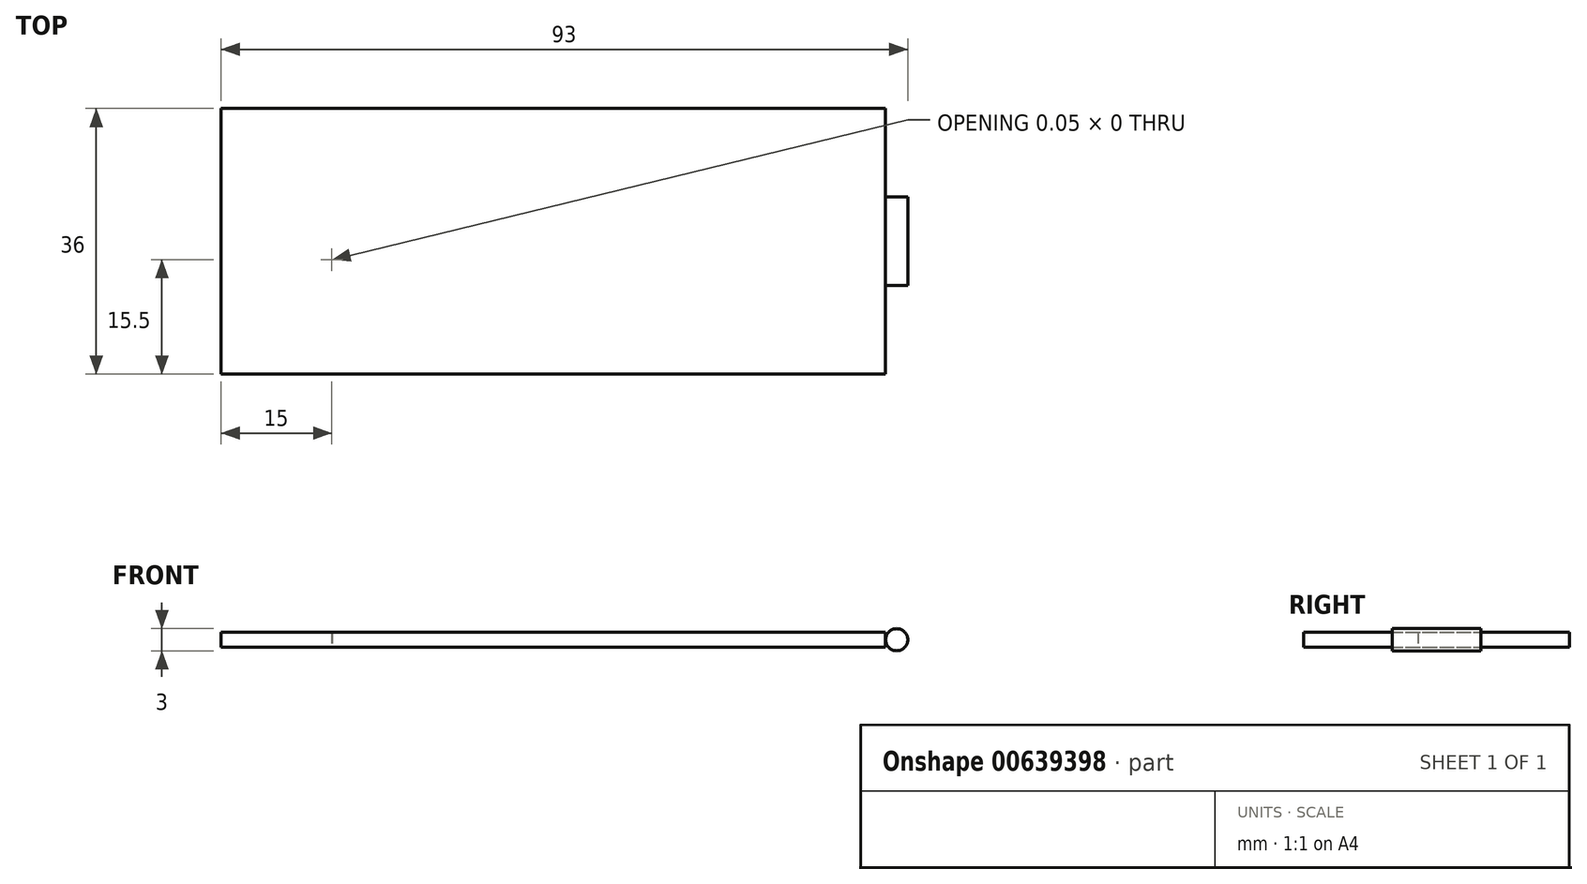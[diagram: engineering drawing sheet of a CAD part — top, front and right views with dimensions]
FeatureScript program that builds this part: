
annotation { "Feature Type Name" : "Feature", "Feature Type Description" : "" }
export const myFeature = defineFeature(function(context is Context, id is Id, definition is map)
    precondition{}
    {
        {
            var Q0;
            Q0=qCreatedBy(makeId("Top.planeOp"),FACE);
            var sketch = newSketch(context, id + "F0", { "sketchPlane" : qUnion([Q0])});
            skLineSegment(sketch, "E0.bottom", {"start": v(0, 0) * mm, "end": v(90, 0) * mm});
            skLineSegment(sketch, "E0.top", {"start": v(0, 36) * mm, "end": v(90, 36) * mm});
            skLineSegment(sketch, "E0.left", {"start": v(0, 0) * mm, "end": v(0, 36) * mm});
            skLineSegment(sketch, "E0.right", {"start": v(90, 0) * mm, "end": v(90, 36) * mm});
            skSolve(sketch);
        }
        {
            var Q0;
            Q0=makeQuery(id+"F0.imprint","IMPRINT",FACE,{"disambiguationData":[TD([[makeQuery(id+"F0.imprint","IMPRINT",EDGE,{"derivedFrom":sQuery(id+"F0.wireOp",EDGE,"E0.bottom")}),1.0]])]});
            extrude(context, id + "F1", {"entities" : qUnion([Q0]), "depth" : 2 * mm, "offsetDistance" : 25 * mm});
        }
        {
            var Q0;
            Q0=qCreatedBy(makeId("Front.planeOp"),FACE);
            cPlane(context, id + "F2", {"entities" : qUnion([Q0]), "cplaneType" : CPlaneType.OFFSET, "offset" : 18 * mm, "oppositeDirection" : true, "width" : 150 * mm, "height" : 150 * mm});
        }
        {
            var Q0;
            Q0=qCreatedBy(id+"F2.planeOp",FACE);
            var sketch = newSketch(context, id + "F3", { "sketchPlane" : qUnion([Q0])});
            skPoint(sketch, "E1.0", {"position": v(90, 1) * mm});
            skCircle(sketch, "E2", {"center": v(91.5, 1) * mm, "radius": 1.5 * mm});
            skSolve(sketch);
        }
        {
            var Q0;
            Q0=makeQuery(id+"F3.imprint","IMPRINT",FACE,{"disambiguationData":[TD([[makeQuery(id+"F3.imprint","IMPRINT",EDGE,{"derivedFrom":sQuery(id+"F3.wireOp",EDGE,"E2")}),1.0]])]});
            extrude(context, id + "F4", {"entities" : qUnion([Q0]), "operationType" : NewBodyOperationType.ADD, "depth" : 12 * mm, "offsetDistance" : 25 * mm, "symmetric" : true});
        }
        {
            var Q0;
            Q0=makeQuery(id+"F1.opExtrude","CAP_FACE",FACE,{"disambiguationData":[OSD([sQuery(id+"F0.wireOp",EDGE,"E0.bottom"),sQuery(id+"F0.wireOp",EDGE,"E0.top"),sQuery(id+"F0.wireOp",EDGE,"E0.left"),sQuery(id+"F0.wireOp",EDGE,"E0.right")])],"isStart":true});
            var sketch = newSketch(context, id + "F5", { "sketchPlane" : qUnion([Q0])});
            skLineSegment(sketch, "E3.0", {"start": v(0, 0) * mm, "end": v(0, -36) * mm});
            skArc(sketch, "E4", {"start": v(15.02, -15.5) * mm, "mid": v(12.5, -17.99) * mm, "end": v(15, -20.5) * mm});
            skPoint(sketch, "E4.centerSnap0", {"position": v(0, -18) * mm});
            skArc(sketch, "E5", {"start": v(29.76, -20.49) * mm, "mid": v(32.5, -18.1) * mm, "end": v(29.98, -15.5) * mm});
            skLineSegment(sketch, "E6", {"start": v(29.98, -15.5) * mm, "end": v(14.98, -15.5) * mm});
            skLineSegment(sketch, "E7", {"start": v(29.76, -20.49) * mm, "end": v(15, -20.5) * mm});
            skSolve(sketch);
        }
        {
            var Q0;
            {var subQ1=sQuery(id+"F5.wireOp",EDGE,"E4");Q0=makeQuery(id+"F5.imprint","IMPRINT",FACE,{"disambiguationData":[TD([[makeQuery(id+"F5.imprint","IMPRINT",EDGE,{"derivedFrom":subQ1}),1.0]])]});}
            extrude(context, id + "F6", {"entities" : qUnion([Q0]), "operationType" : NewBodyOperationType.REMOVE, "endBound" : BoundingType.UP_TO_NEXT, "oppositeDirection" : true, "depth" : 25 * mm, "offsetDistance" : 25 * mm});
        }
    });
